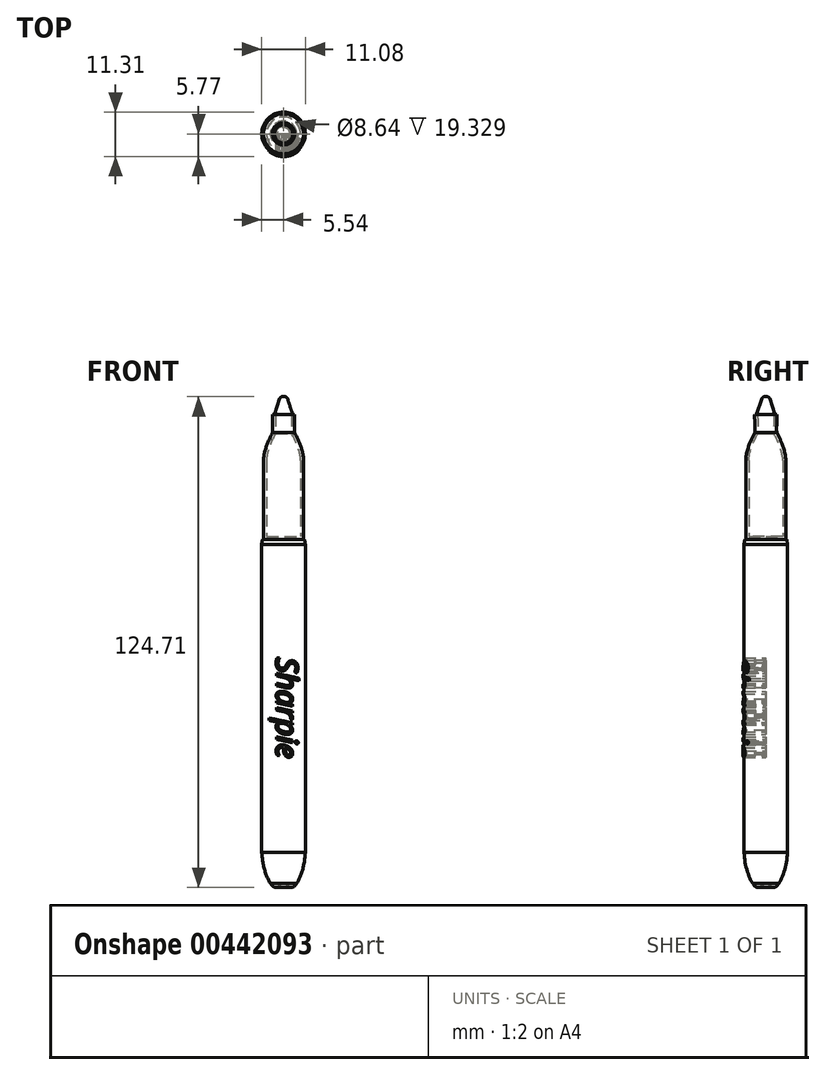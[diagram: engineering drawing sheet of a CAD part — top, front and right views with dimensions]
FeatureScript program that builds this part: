
annotation { "Feature Type Name" : "Feature", "Feature Type Description" : "" }
export const myFeature = defineFeature(function(context is Context, id is Id, definition is map)
    precondition{}
    {
        {
            var Q0;
            Q0=qCreatedBy(makeId("Right.planeOp"),FACE);
            var sketch = newSketch(context, id + "F0", { "sketchPlane" : qUnion([Q0])});
            skArc(sketch, "E0", {"start": v(1.65, 0) * mm, "mid": v(0.9, 0.63) * mm, "end": v(0, 1.02) * mm});
            skLineSegment(sketch, "E1", {"start": v(0, 0) * mm, "end": v(0, 15.3) * mm, "construction": true});
            skLineSegment(sketch, "E2", {"start": v(-4.14, 8.9) * mm, "end": v(12.15, 8.9) * mm, "construction": true});
            skLineSegment(sketch, "E3", {"start": v(5.54, -3.16) * mm, "end": v(5.54, 13.42) * mm, "construction": true});
            skLineSegment(sketch, "E4", {"start": v(3.31, 16.2) * mm, "end": v(3.31, -2.19) * mm, "construction": true});
            skFitSpline(sketch, "E5", {"points": [v(1.65, 0) * mm, v(3.31, 1.03) * mm], "startDerivative": vector(2.74, 0) * mm, "endDerivative": vector(1.4, 2.31) * mm});
            skFitSpline(sketch, "E6", {"points": [v(3.31, 1.03) * mm, v(5.54, 8.9) * mm], "startDerivative": vector(3.92, 5.98) * mm, "endDerivative": vector(0.67, 9.24) * mm});
            skLineSegment(sketch, "E7", {"start": v(-15.24, 87.12) * mm, "end": v(35.45, 87.12) * mm, "construction": true});
            skLineSegment(sketch, "E8", {"start": v(5.54, 8.9) * mm, "end": v(5.54, 87.12) * mm});
            skPoint(sketch, "E8.endSnap0", {"position": v(10.1, 87.12) * mm});
            skLineSegment(sketch, "E9", {"start": v(5.54, 87.12) * mm, "end": v(5.33, 88.38) * mm});
            skLineSegment(sketch, "E10", {"start": v(5.33, 88.38) * mm, "end": v(0, 88.38) * mm});
            skLineSegment(sketch, "E11", {"start": v(0, 88.38) * mm, "end": v(0, 1.02) * mm});
            skSolve(sketch);
        }
        {
            var Q0;
            Q0=qSketchRegion(id+"F0",true);
            var Q1;
            Q1=sQuery(id+"F0.wireOp",EDGE,"E11");
            revolve(context, id + "F1", {"entities" : qUnion([Q0]), "axis" : qUnion([Q1]), "revolveType" : RevolveType.FULL});
        }
        {
            var Q0;
            Q0=qCreatedBy(makeId("Front.planeOp"),FACE);
            var sketch = newSketch(context, id + "F2", { "sketchPlane" : qUnion([Q0])});
            skLineSegment(sketch, "E12", {"start": v(0, 88.38) * mm, "end": v(0, 120.13) * mm});
            skLineSegment(sketch, "E13", {"start": v(0, 120.13) * mm, "end": v(2.8, 120.13) * mm});
            skLineSegment(sketch, "E14", {"start": v(-7.77, 108.47) * mm, "end": v(20.65, 108.47) * mm, "construction": true});
            skLineSegment(sketch, "E15", {"start": v(5.08, 128.73) * mm, "end": v(5.08, 79.74) * mm, "construction": true});
            skLineSegment(sketch, "E16", {"start": v(5.08, 79.74) * mm, "end": v(5.61, 79.74) * mm, "construction": true});
            skLineSegment(sketch, "E17", {"start": v(0, 88.38) * mm, "end": v(5.08, 88.38) * mm});
            skLineSegment(sketch, "E18", {"start": v(5.08, 88.38) * mm, "end": v(5.08, 108.47) * mm});
            skFitSpline(sketch, "E19", {"points": [v(2.8, 115.55) * mm, v(5.08, 108.47) * mm], "startDerivative": vector(4.16, -7.76) * mm, "endDerivative": vector(0, -5.98) * mm});
            skFitSpline(sketch, "E20", {"points": [v(2.8, 120.13) * mm, v(2.8, 115.55) * mm], "startDerivative": vector(0.35, -1.11) * mm, "endDerivative": vector(0.39, -3.2) * mm});
            skSolve(sketch);
        }
        {
            var Q0;
            Q0=makeQuery(id+"F2.imprint","IMPRINT",FACE,{"disambiguationData":[TD([[makeQuery(id+"F2.imprint","IMPRINT",EDGE,{"derivedFrom":sQuery(id+"F2.wireOp",EDGE,"E12")}),-1.0]])]});
            var Q1;
            Q1=sQuery(id+"F2.wireOp",EDGE,"E12");
            revolve(context, id + "F3", {"entities" : qUnion([Q0]), "axis" : qUnion([Q1]), "revolveType" : RevolveType.FULL});
        }
        {
            var Q0;
            Q0=makeQuery(id+"F3.opRevolve","SWEPT_FACE",FACE,{"disambiguationData":[OSD([sQuery(id+"F2.wireOp",EDGE,"E13")])]});
            shell(context, id + "F4", {"entities" : qUnion([Q0]), "thickness" : 0.76 * mm});
        }
        {
            var Q0;
            Q0=qCreatedBy(makeId("Front.planeOp"),FACE);
            var sketch = newSketch(context, id + "F5", { "sketchPlane" : qUnion([Q0])});
            skText(sketch, "E21", { "text": "Sharpie", "fontName": "OpenSans-Italic.ttf"});
            const initialGuessF5  = {"E21": [-0.00997, 0.02356, 1, 0, 0.00548]};
            skSetInitialGuess(sketch, initialGuessF5);
            skSolve(sketch);
        }
        {
            var Q0;
            Q0=qSketchRegion(id+"F5",true);
            extrude(context, id + "F6", {"entities" : qUnion([Q0]), "depth" : 6.35 * mm});
        }
        {
            var Q0;
            Q0=qCreatedBy(makeId("Front.planeOp"),FACE);
            var sketch = newSketch(context, id + "F7", { "sketchPlane" : qUnion([Q0])});
            skLineSegment(sketch, "E22", {"start": v(0, 0) * mm, "end": v(0, 153.56) * mm, "construction": true});
            skLineSegment(sketch, "E23", {"start": v(0, 0) * mm, "end": v(-98.51, 0) * mm, "construction": true});
            skSolve(sketch);
        }
        {
            var Q0;
            Q0=qCreatedBy(makeId("Top.planeOp"),FACE);
            var sketch = newSketch(context, id + "F8", { "sketchPlane" : qUnion([Q0])});
            skLineSegment(sketch, "E24", {"start": v(0, 0) * mm, "end": v(0, 70.55) * mm, "construction": true});
            skSolve(sketch);
        }
        {
            var Q0;
            Q0=makeQuery(id+"F6.opExtrude","SWEPT_BODY",BODY,{"disambiguationData":[OSD([sQuery(id+"F5.wireOp",EDGE,"E21.sketch_text.stroke-126"),sQuery(id+"F5.wireOp",EDGE,"E21.sketch_text.stroke-127"),sQuery(id+"F5.wireOp",EDGE,"E21.sketch_text.stroke-128"),sQuery(id+"F5.wireOp",EDGE,"E21.sketch_text.stroke-129"),sQuery(id+"F5.wireOp",EDGE,"E21.sketch_text.stroke-130"),sQuery(id+"F5.wireOp",EDGE,"E21.sketch_text.stroke-131"),sQuery(id+"F5.wireOp",EDGE,"E21.sketch_text.stroke-132"),sQuery(id+"F5.wireOp",EDGE,"E21.sketch_text.stroke-133"),sQuery(id+"F5.wireOp",EDGE,"E21.sketch_text.stroke-134"),sQuery(id+"F5.wireOp",EDGE,"E21.sketch_text.stroke-135"),sQuery(id+"F5.wireOp",EDGE,"E21.sketch_text.stroke-136"),sQuery(id+"F5.wireOp",EDGE,"E21.sketch_text.stroke-137"),sQuery(id+"F5.wireOp",EDGE,"E21.sketch_text.stroke-138"),sQuery(id+"F5.wireOp",EDGE,"E21.sketch_text.stroke-139"),sQuery(id+"F5.wireOp",EDGE,"E21.sketch_text.stroke-140"),sQuery(id+"F5.wireOp",EDGE,"E21.sketch_text.stroke-141"),sQuery(id+"F5.wireOp",EDGE,"E21.sketch_text.stroke-142"),sQuery(id+"F5.wireOp",EDGE,"E21.sketch_text.stroke-143"),sQuery(id+"F5.wireOp",EDGE,"E21.sketch_text.stroke-144"),sQuery(id+"F5.wireOp",EDGE,"E21.sketch_text.stroke-145"),sQuery(id+"F5.wireOp",EDGE,"E21.sketch_text.stroke-146"),sQuery(id+"F5.wireOp",EDGE,"E21.sketch_text.stroke-147"),sQuery(id+"F5.wireOp",EDGE,"E21.sketch_text.stroke-148"),sQuery(id+"F5.wireOp",EDGE,"E21.sketch_text.stroke-149"),sQuery(id+"F5.wireOp",EDGE,"E21.sketch_text.stroke-150")])]});
            var Q1;
            Q1=makeQuery(id+"F6.opExtrude","SWEPT_BODY",BODY,{"disambiguationData":[OSD([sQuery(id+"F5.wireOp",EDGE,"E21.sketch_text.stroke-119"),sQuery(id+"F5.wireOp",EDGE,"E21.sketch_text.stroke-120"),sQuery(id+"F5.wireOp",EDGE,"E21.sketch_text.stroke-121"),sQuery(id+"F5.wireOp",EDGE,"E21.sketch_text.stroke-122"),sQuery(id+"F5.wireOp",EDGE,"E21.sketch_text.stroke-123"),sQuery(id+"F5.wireOp",EDGE,"E21.sketch_text.stroke-124"),sQuery(id+"F5.wireOp",EDGE,"E21.sketch_text.stroke-125")])]});
            var Q2;
            Q2=makeQuery(id+"F6.opExtrude","SWEPT_BODY",BODY,{"disambiguationData":[OSD([sQuery(id+"F5.wireOp",EDGE,"E21.sketch_text.stroke-115"),sQuery(id+"F5.wireOp",EDGE,"E21.sketch_text.stroke-116"),sQuery(id+"F5.wireOp",EDGE,"E21.sketch_text.stroke-117"),sQuery(id+"F5.wireOp",EDGE,"E21.sketch_text.stroke-118")])]});
            var Q3;
            Q3=makeQuery(id+"F6.opExtrude","SWEPT_BODY",BODY,{"disambiguationData":[OSD([sQuery(id+"F5.wireOp",EDGE,"E21.sketch_text.stroke-89"),sQuery(id+"F5.wireOp",EDGE,"E21.sketch_text.stroke-90"),sQuery(id+"F5.wireOp",EDGE,"E21.sketch_text.stroke-91"),sQuery(id+"F5.wireOp",EDGE,"E21.sketch_text.stroke-92"),sQuery(id+"F5.wireOp",EDGE,"E21.sketch_text.stroke-93"),sQuery(id+"F5.wireOp",EDGE,"E21.sketch_text.stroke-94"),sQuery(id+"F5.wireOp",EDGE,"E21.sketch_text.stroke-95"),sQuery(id+"F5.wireOp",EDGE,"E21.sketch_text.stroke-96"),sQuery(id+"F5.wireOp",EDGE,"E21.sketch_text.stroke-97"),sQuery(id+"F5.wireOp",EDGE,"E21.sketch_text.stroke-98"),sQuery(id+"F5.wireOp",EDGE,"E21.sketch_text.stroke-99"),sQuery(id+"F5.wireOp",EDGE,"E21.sketch_text.stroke-100"),sQuery(id+"F5.wireOp",EDGE,"E21.sketch_text.stroke-101"),sQuery(id+"F5.wireOp",EDGE,"E21.sketch_text.stroke-102"),sQuery(id+"F5.wireOp",EDGE,"E21.sketch_text.stroke-103"),sQuery(id+"F5.wireOp",EDGE,"E21.sketch_text.stroke-104"),sQuery(id+"F5.wireOp",EDGE,"E21.sketch_text.stroke-105"),sQuery(id+"F5.wireOp",EDGE,"E21.sketch_text.stroke-106"),sQuery(id+"F5.wireOp",EDGE,"E21.sketch_text.stroke-107"),sQuery(id+"F5.wireOp",EDGE,"E21.sketch_text.stroke-108"),sQuery(id+"F5.wireOp",EDGE,"E21.sketch_text.stroke-109"),sQuery(id+"F5.wireOp",EDGE,"E21.sketch_text.stroke-110"),sQuery(id+"F5.wireOp",EDGE,"E21.sketch_text.stroke-111"),sQuery(id+"F5.wireOp",EDGE,"E21.sketch_text.stroke-112"),sQuery(id+"F5.wireOp",EDGE,"E21.sketch_text.stroke-113"),sQuery(id+"F5.wireOp",EDGE,"E21.sketch_text.stroke-114")])]});
            var Q4;
            Q4=makeQuery(id+"F6.opExtrude","SWEPT_BODY",BODY,{"disambiguationData":[OSD([sQuery(id+"F5.wireOp",EDGE,"E21.sketch_text.stroke-74"),sQuery(id+"F5.wireOp",EDGE,"E21.sketch_text.stroke-75"),sQuery(id+"F5.wireOp",EDGE,"E21.sketch_text.stroke-76"),sQuery(id+"F5.wireOp",EDGE,"E21.sketch_text.stroke-77"),sQuery(id+"F5.wireOp",EDGE,"E21.sketch_text.stroke-78"),sQuery(id+"F5.wireOp",EDGE,"E21.sketch_text.stroke-79"),sQuery(id+"F5.wireOp",EDGE,"E21.sketch_text.stroke-80"),sQuery(id+"F5.wireOp",EDGE,"E21.sketch_text.stroke-81"),sQuery(id+"F5.wireOp",EDGE,"E21.sketch_text.stroke-82"),sQuery(id+"F5.wireOp",EDGE,"E21.sketch_text.stroke-83"),sQuery(id+"F5.wireOp",EDGE,"E21.sketch_text.stroke-84"),sQuery(id+"F5.wireOp",EDGE,"E21.sketch_text.stroke-85"),sQuery(id+"F5.wireOp",EDGE,"E21.sketch_text.stroke-86"),sQuery(id+"F5.wireOp",EDGE,"E21.sketch_text.stroke-87"),sQuery(id+"F5.wireOp",EDGE,"E21.sketch_text.stroke-88")])]});
            var Q5;
            Q5=makeQuery(id+"F6.opExtrude","SWEPT_BODY",BODY,{"disambiguationData":[OSD([sQuery(id+"F5.wireOp",EDGE,"E21.sketch_text.stroke-49"),sQuery(id+"F5.wireOp",EDGE,"E21.sketch_text.stroke-50"),sQuery(id+"F5.wireOp",EDGE,"E21.sketch_text.stroke-51"),sQuery(id+"F5.wireOp",EDGE,"E21.sketch_text.stroke-52"),sQuery(id+"F5.wireOp",EDGE,"E21.sketch_text.stroke-53"),sQuery(id+"F5.wireOp",EDGE,"E21.sketch_text.stroke-54"),sQuery(id+"F5.wireOp",EDGE,"E21.sketch_text.stroke-55"),sQuery(id+"F5.wireOp",EDGE,"E21.sketch_text.stroke-56"),sQuery(id+"F5.wireOp",EDGE,"E21.sketch_text.stroke-57"),sQuery(id+"F5.wireOp",EDGE,"E21.sketch_text.stroke-58"),sQuery(id+"F5.wireOp",EDGE,"E21.sketch_text.stroke-59"),sQuery(id+"F5.wireOp",EDGE,"E21.sketch_text.stroke-60"),sQuery(id+"F5.wireOp",EDGE,"E21.sketch_text.stroke-61"),sQuery(id+"F5.wireOp",EDGE,"E21.sketch_text.stroke-62"),sQuery(id+"F5.wireOp",EDGE,"E21.sketch_text.stroke-63"),sQuery(id+"F5.wireOp",EDGE,"E21.sketch_text.stroke-64"),sQuery(id+"F5.wireOp",EDGE,"E21.sketch_text.stroke-65"),sQuery(id+"F5.wireOp",EDGE,"E21.sketch_text.stroke-66"),sQuery(id+"F5.wireOp",EDGE,"E21.sketch_text.stroke-67"),sQuery(id+"F5.wireOp",EDGE,"E21.sketch_text.stroke-68"),sQuery(id+"F5.wireOp",EDGE,"E21.sketch_text.stroke-69"),sQuery(id+"F5.wireOp",EDGE,"E21.sketch_text.stroke-70"),sQuery(id+"F5.wireOp",EDGE,"E21.sketch_text.stroke-71"),sQuery(id+"F5.wireOp",EDGE,"E21.sketch_text.stroke-72"),sQuery(id+"F5.wireOp",EDGE,"E21.sketch_text.stroke-73")])]});
            var Q6;
            Q6=makeQuery(id+"F6.opExtrude","SWEPT_BODY",BODY,{"disambiguationData":[OSD([sQuery(id+"F5.wireOp",EDGE,"E21.sketch_text.stroke-27"),sQuery(id+"F5.wireOp",EDGE,"E21.sketch_text.stroke-28"),sQuery(id+"F5.wireOp",EDGE,"E21.sketch_text.stroke-29"),sQuery(id+"F5.wireOp",EDGE,"E21.sketch_text.stroke-30"),sQuery(id+"F5.wireOp",EDGE,"E21.sketch_text.stroke-31"),sQuery(id+"F5.wireOp",EDGE,"E21.sketch_text.stroke-32"),sQuery(id+"F5.wireOp",EDGE,"E21.sketch_text.stroke-33"),sQuery(id+"F5.wireOp",EDGE,"E21.sketch_text.stroke-34"),sQuery(id+"F5.wireOp",EDGE,"E21.sketch_text.stroke-35"),sQuery(id+"F5.wireOp",EDGE,"E21.sketch_text.stroke-36"),sQuery(id+"F5.wireOp",EDGE,"E21.sketch_text.stroke-37"),sQuery(id+"F5.wireOp",EDGE,"E21.sketch_text.stroke-38"),sQuery(id+"F5.wireOp",EDGE,"E21.sketch_text.stroke-39"),sQuery(id+"F5.wireOp",EDGE,"E21.sketch_text.stroke-40"),sQuery(id+"F5.wireOp",EDGE,"E21.sketch_text.stroke-41"),sQuery(id+"F5.wireOp",EDGE,"E21.sketch_text.stroke-42"),sQuery(id+"F5.wireOp",EDGE,"E21.sketch_text.stroke-43"),sQuery(id+"F5.wireOp",EDGE,"E21.sketch_text.stroke-44"),sQuery(id+"F5.wireOp",EDGE,"E21.sketch_text.stroke-45"),sQuery(id+"F5.wireOp",EDGE,"E21.sketch_text.stroke-46"),sQuery(id+"F5.wireOp",EDGE,"E21.sketch_text.stroke-47"),sQuery(id+"F5.wireOp",EDGE,"E21.sketch_text.stroke-48")])]});
            var Q7;
            Q7=makeQuery(id+"F6.opExtrude","SWEPT_BODY",BODY,{"disambiguationData":[OSD([sQuery(id+"F5.wireOp",EDGE,"E21.sketch_text.stroke-0"),sQuery(id+"F5.wireOp",EDGE,"E21.sketch_text.stroke-1"),sQuery(id+"F5.wireOp",EDGE,"E21.sketch_text.stroke-2"),sQuery(id+"F5.wireOp",EDGE,"E21.sketch_text.stroke-3"),sQuery(id+"F5.wireOp",EDGE,"E21.sketch_text.stroke-4"),sQuery(id+"F5.wireOp",EDGE,"E21.sketch_text.stroke-5"),sQuery(id+"F5.wireOp",EDGE,"E21.sketch_text.stroke-6"),sQuery(id+"F5.wireOp",EDGE,"E21.sketch_text.stroke-7"),sQuery(id+"F5.wireOp",EDGE,"E21.sketch_text.stroke-8"),sQuery(id+"F5.wireOp",EDGE,"E21.sketch_text.stroke-9"),sQuery(id+"F5.wireOp",EDGE,"E21.sketch_text.stroke-10"),sQuery(id+"F5.wireOp",EDGE,"E21.sketch_text.stroke-11"),sQuery(id+"F5.wireOp",EDGE,"E21.sketch_text.stroke-12"),sQuery(id+"F5.wireOp",EDGE,"E21.sketch_text.stroke-13"),sQuery(id+"F5.wireOp",EDGE,"E21.sketch_text.stroke-14"),sQuery(id+"F5.wireOp",EDGE,"E21.sketch_text.stroke-15"),sQuery(id+"F5.wireOp",EDGE,"E21.sketch_text.stroke-16"),sQuery(id+"F5.wireOp",EDGE,"E21.sketch_text.stroke-17"),sQuery(id+"F5.wireOp",EDGE,"E21.sketch_text.stroke-18"),sQuery(id+"F5.wireOp",EDGE,"E21.sketch_text.stroke-19"),sQuery(id+"F5.wireOp",EDGE,"E21.sketch_text.stroke-20"),sQuery(id+"F5.wireOp",EDGE,"E21.sketch_text.stroke-21"),sQuery(id+"F5.wireOp",EDGE,"E21.sketch_text.stroke-22"),sQuery(id+"F5.wireOp",EDGE,"E21.sketch_text.stroke-23"),sQuery(id+"F5.wireOp",EDGE,"E21.sketch_text.stroke-24"),sQuery(id+"F5.wireOp",EDGE,"E21.sketch_text.stroke-25"),sQuery(id+"F5.wireOp",EDGE,"E21.sketch_text.stroke-26")])]});
            var Q8;
            Q8=sQuery(id+"F8.wireOp",EDGE,"E24");
            transform(context, id + "F9", {"entities" : qUnion([Q0, Q1, Q2, Q3, Q4, Q5, Q6, Q7]), "transformType" : TransformType.ROTATION, "transformAxis" : qUnion([Q8]), "angle" : 90 * degree, "makeCopy" : false});
        }
        {
            var Q0;
            Q0=makeQuery(id+"F6.opExtrude","SWEPT_BODY",BODY,{"disambiguationData":[OSD([sQuery(id+"F5.wireOp",EDGE,"E21.sketch_text.stroke-0"),sQuery(id+"F5.wireOp",EDGE,"E21.sketch_text.stroke-1"),sQuery(id+"F5.wireOp",EDGE,"E21.sketch_text.stroke-2"),sQuery(id+"F5.wireOp",EDGE,"E21.sketch_text.stroke-3"),sQuery(id+"F5.wireOp",EDGE,"E21.sketch_text.stroke-4"),sQuery(id+"F5.wireOp",EDGE,"E21.sketch_text.stroke-5"),sQuery(id+"F5.wireOp",EDGE,"E21.sketch_text.stroke-6"),sQuery(id+"F5.wireOp",EDGE,"E21.sketch_text.stroke-7"),sQuery(id+"F5.wireOp",EDGE,"E21.sketch_text.stroke-8"),sQuery(id+"F5.wireOp",EDGE,"E21.sketch_text.stroke-9"),sQuery(id+"F5.wireOp",EDGE,"E21.sketch_text.stroke-10"),sQuery(id+"F5.wireOp",EDGE,"E21.sketch_text.stroke-11"),sQuery(id+"F5.wireOp",EDGE,"E21.sketch_text.stroke-12"),sQuery(id+"F5.wireOp",EDGE,"E21.sketch_text.stroke-13"),sQuery(id+"F5.wireOp",EDGE,"E21.sketch_text.stroke-14"),sQuery(id+"F5.wireOp",EDGE,"E21.sketch_text.stroke-15"),sQuery(id+"F5.wireOp",EDGE,"E21.sketch_text.stroke-16"),sQuery(id+"F5.wireOp",EDGE,"E21.sketch_text.stroke-17"),sQuery(id+"F5.wireOp",EDGE,"E21.sketch_text.stroke-18"),sQuery(id+"F5.wireOp",EDGE,"E21.sketch_text.stroke-19"),sQuery(id+"F5.wireOp",EDGE,"E21.sketch_text.stroke-20"),sQuery(id+"F5.wireOp",EDGE,"E21.sketch_text.stroke-21"),sQuery(id+"F5.wireOp",EDGE,"E21.sketch_text.stroke-22"),sQuery(id+"F5.wireOp",EDGE,"E21.sketch_text.stroke-23"),sQuery(id+"F5.wireOp",EDGE,"E21.sketch_text.stroke-24"),sQuery(id+"F5.wireOp",EDGE,"E21.sketch_text.stroke-25"),sQuery(id+"F5.wireOp",EDGE,"E21.sketch_text.stroke-26")])]});
            var Q1;
            Q1=makeQuery(id+"F6.opExtrude","SWEPT_BODY",BODY,{"disambiguationData":[OSD([sQuery(id+"F5.wireOp",EDGE,"E21.sketch_text.stroke-27"),sQuery(id+"F5.wireOp",EDGE,"E21.sketch_text.stroke-28"),sQuery(id+"F5.wireOp",EDGE,"E21.sketch_text.stroke-29"),sQuery(id+"F5.wireOp",EDGE,"E21.sketch_text.stroke-30"),sQuery(id+"F5.wireOp",EDGE,"E21.sketch_text.stroke-31"),sQuery(id+"F5.wireOp",EDGE,"E21.sketch_text.stroke-32"),sQuery(id+"F5.wireOp",EDGE,"E21.sketch_text.stroke-33"),sQuery(id+"F5.wireOp",EDGE,"E21.sketch_text.stroke-34"),sQuery(id+"F5.wireOp",EDGE,"E21.sketch_text.stroke-35"),sQuery(id+"F5.wireOp",EDGE,"E21.sketch_text.stroke-36"),sQuery(id+"F5.wireOp",EDGE,"E21.sketch_text.stroke-37"),sQuery(id+"F5.wireOp",EDGE,"E21.sketch_text.stroke-38"),sQuery(id+"F5.wireOp",EDGE,"E21.sketch_text.stroke-39"),sQuery(id+"F5.wireOp",EDGE,"E21.sketch_text.stroke-40"),sQuery(id+"F5.wireOp",EDGE,"E21.sketch_text.stroke-41"),sQuery(id+"F5.wireOp",EDGE,"E21.sketch_text.stroke-42"),sQuery(id+"F5.wireOp",EDGE,"E21.sketch_text.stroke-43"),sQuery(id+"F5.wireOp",EDGE,"E21.sketch_text.stroke-44"),sQuery(id+"F5.wireOp",EDGE,"E21.sketch_text.stroke-45"),sQuery(id+"F5.wireOp",EDGE,"E21.sketch_text.stroke-46"),sQuery(id+"F5.wireOp",EDGE,"E21.sketch_text.stroke-47"),sQuery(id+"F5.wireOp",EDGE,"E21.sketch_text.stroke-48")])]});
            var Q2;
            Q2=makeQuery(id+"F6.opExtrude","SWEPT_BODY",BODY,{"disambiguationData":[OSD([sQuery(id+"F5.wireOp",EDGE,"E21.sketch_text.stroke-49"),sQuery(id+"F5.wireOp",EDGE,"E21.sketch_text.stroke-50"),sQuery(id+"F5.wireOp",EDGE,"E21.sketch_text.stroke-51"),sQuery(id+"F5.wireOp",EDGE,"E21.sketch_text.stroke-52"),sQuery(id+"F5.wireOp",EDGE,"E21.sketch_text.stroke-53"),sQuery(id+"F5.wireOp",EDGE,"E21.sketch_text.stroke-54"),sQuery(id+"F5.wireOp",EDGE,"E21.sketch_text.stroke-55"),sQuery(id+"F5.wireOp",EDGE,"E21.sketch_text.stroke-56"),sQuery(id+"F5.wireOp",EDGE,"E21.sketch_text.stroke-57"),sQuery(id+"F5.wireOp",EDGE,"E21.sketch_text.stroke-58"),sQuery(id+"F5.wireOp",EDGE,"E21.sketch_text.stroke-59"),sQuery(id+"F5.wireOp",EDGE,"E21.sketch_text.stroke-60"),sQuery(id+"F5.wireOp",EDGE,"E21.sketch_text.stroke-61"),sQuery(id+"F5.wireOp",EDGE,"E21.sketch_text.stroke-62"),sQuery(id+"F5.wireOp",EDGE,"E21.sketch_text.stroke-63"),sQuery(id+"F5.wireOp",EDGE,"E21.sketch_text.stroke-64"),sQuery(id+"F5.wireOp",EDGE,"E21.sketch_text.stroke-65"),sQuery(id+"F5.wireOp",EDGE,"E21.sketch_text.stroke-66"),sQuery(id+"F5.wireOp",EDGE,"E21.sketch_text.stroke-67"),sQuery(id+"F5.wireOp",EDGE,"E21.sketch_text.stroke-68"),sQuery(id+"F5.wireOp",EDGE,"E21.sketch_text.stroke-69"),sQuery(id+"F5.wireOp",EDGE,"E21.sketch_text.stroke-70"),sQuery(id+"F5.wireOp",EDGE,"E21.sketch_text.stroke-71"),sQuery(id+"F5.wireOp",EDGE,"E21.sketch_text.stroke-72"),sQuery(id+"F5.wireOp",EDGE,"E21.sketch_text.stroke-73")])]});
            var Q3;
            Q3=makeQuery(id+"F6.opExtrude","SWEPT_BODY",BODY,{"disambiguationData":[OSD([sQuery(id+"F5.wireOp",EDGE,"E21.sketch_text.stroke-74"),sQuery(id+"F5.wireOp",EDGE,"E21.sketch_text.stroke-75"),sQuery(id+"F5.wireOp",EDGE,"E21.sketch_text.stroke-76"),sQuery(id+"F5.wireOp",EDGE,"E21.sketch_text.stroke-77"),sQuery(id+"F5.wireOp",EDGE,"E21.sketch_text.stroke-78"),sQuery(id+"F5.wireOp",EDGE,"E21.sketch_text.stroke-79"),sQuery(id+"F5.wireOp",EDGE,"E21.sketch_text.stroke-80"),sQuery(id+"F5.wireOp",EDGE,"E21.sketch_text.stroke-81"),sQuery(id+"F5.wireOp",EDGE,"E21.sketch_text.stroke-82"),sQuery(id+"F5.wireOp",EDGE,"E21.sketch_text.stroke-83"),sQuery(id+"F5.wireOp",EDGE,"E21.sketch_text.stroke-84"),sQuery(id+"F5.wireOp",EDGE,"E21.sketch_text.stroke-85"),sQuery(id+"F5.wireOp",EDGE,"E21.sketch_text.stroke-86"),sQuery(id+"F5.wireOp",EDGE,"E21.sketch_text.stroke-87"),sQuery(id+"F5.wireOp",EDGE,"E21.sketch_text.stroke-88")])]});
            var Q4;
            Q4=makeQuery(id+"F6.opExtrude","SWEPT_BODY",BODY,{"disambiguationData":[OSD([sQuery(id+"F5.wireOp",EDGE,"E21.sketch_text.stroke-89"),sQuery(id+"F5.wireOp",EDGE,"E21.sketch_text.stroke-90"),sQuery(id+"F5.wireOp",EDGE,"E21.sketch_text.stroke-91"),sQuery(id+"F5.wireOp",EDGE,"E21.sketch_text.stroke-92"),sQuery(id+"F5.wireOp",EDGE,"E21.sketch_text.stroke-93"),sQuery(id+"F5.wireOp",EDGE,"E21.sketch_text.stroke-94"),sQuery(id+"F5.wireOp",EDGE,"E21.sketch_text.stroke-95"),sQuery(id+"F5.wireOp",EDGE,"E21.sketch_text.stroke-96"),sQuery(id+"F5.wireOp",EDGE,"E21.sketch_text.stroke-97"),sQuery(id+"F5.wireOp",EDGE,"E21.sketch_text.stroke-98"),sQuery(id+"F5.wireOp",EDGE,"E21.sketch_text.stroke-99"),sQuery(id+"F5.wireOp",EDGE,"E21.sketch_text.stroke-100"),sQuery(id+"F5.wireOp",EDGE,"E21.sketch_text.stroke-101"),sQuery(id+"F5.wireOp",EDGE,"E21.sketch_text.stroke-102"),sQuery(id+"F5.wireOp",EDGE,"E21.sketch_text.stroke-103"),sQuery(id+"F5.wireOp",EDGE,"E21.sketch_text.stroke-104"),sQuery(id+"F5.wireOp",EDGE,"E21.sketch_text.stroke-105"),sQuery(id+"F5.wireOp",EDGE,"E21.sketch_text.stroke-106"),sQuery(id+"F5.wireOp",EDGE,"E21.sketch_text.stroke-107"),sQuery(id+"F5.wireOp",EDGE,"E21.sketch_text.stroke-108"),sQuery(id+"F5.wireOp",EDGE,"E21.sketch_text.stroke-109"),sQuery(id+"F5.wireOp",EDGE,"E21.sketch_text.stroke-110"),sQuery(id+"F5.wireOp",EDGE,"E21.sketch_text.stroke-111"),sQuery(id+"F5.wireOp",EDGE,"E21.sketch_text.stroke-112"),sQuery(id+"F5.wireOp",EDGE,"E21.sketch_text.stroke-113"),sQuery(id+"F5.wireOp",EDGE,"E21.sketch_text.stroke-114")])]});
            var Q5;
            Q5=makeQuery(id+"F6.opExtrude","SWEPT_BODY",BODY,{"disambiguationData":[OSD([sQuery(id+"F5.wireOp",EDGE,"E21.sketch_text.stroke-115"),sQuery(id+"F5.wireOp",EDGE,"E21.sketch_text.stroke-116"),sQuery(id+"F5.wireOp",EDGE,"E21.sketch_text.stroke-117"),sQuery(id+"F5.wireOp",EDGE,"E21.sketch_text.stroke-118")])]});
            var Q6;
            Q6=makeQuery(id+"F6.opExtrude","SWEPT_BODY",BODY,{"disambiguationData":[OSD([sQuery(id+"F5.wireOp",EDGE,"E21.sketch_text.stroke-119"),sQuery(id+"F5.wireOp",EDGE,"E21.sketch_text.stroke-120"),sQuery(id+"F5.wireOp",EDGE,"E21.sketch_text.stroke-121"),sQuery(id+"F5.wireOp",EDGE,"E21.sketch_text.stroke-122"),sQuery(id+"F5.wireOp",EDGE,"E21.sketch_text.stroke-123"),sQuery(id+"F5.wireOp",EDGE,"E21.sketch_text.stroke-124"),sQuery(id+"F5.wireOp",EDGE,"E21.sketch_text.stroke-125")])]});
            var Q7;
            Q7=makeQuery(id+"F6.opExtrude","SWEPT_BODY",BODY,{"disambiguationData":[OSD([sQuery(id+"F5.wireOp",EDGE,"E21.sketch_text.stroke-126"),sQuery(id+"F5.wireOp",EDGE,"E21.sketch_text.stroke-127"),sQuery(id+"F5.wireOp",EDGE,"E21.sketch_text.stroke-128"),sQuery(id+"F5.wireOp",EDGE,"E21.sketch_text.stroke-129"),sQuery(id+"F5.wireOp",EDGE,"E21.sketch_text.stroke-130"),sQuery(id+"F5.wireOp",EDGE,"E21.sketch_text.stroke-131"),sQuery(id+"F5.wireOp",EDGE,"E21.sketch_text.stroke-132"),sQuery(id+"F5.wireOp",EDGE,"E21.sketch_text.stroke-133"),sQuery(id+"F5.wireOp",EDGE,"E21.sketch_text.stroke-134"),sQuery(id+"F5.wireOp",EDGE,"E21.sketch_text.stroke-135"),sQuery(id+"F5.wireOp",EDGE,"E21.sketch_text.stroke-136"),sQuery(id+"F5.wireOp",EDGE,"E21.sketch_text.stroke-137"),sQuery(id+"F5.wireOp",EDGE,"E21.sketch_text.stroke-138"),sQuery(id+"F5.wireOp",EDGE,"E21.sketch_text.stroke-139"),sQuery(id+"F5.wireOp",EDGE,"E21.sketch_text.stroke-140"),sQuery(id+"F5.wireOp",EDGE,"E21.sketch_text.stroke-141"),sQuery(id+"F5.wireOp",EDGE,"E21.sketch_text.stroke-142"),sQuery(id+"F5.wireOp",EDGE,"E21.sketch_text.stroke-143"),sQuery(id+"F5.wireOp",EDGE,"E21.sketch_text.stroke-144"),sQuery(id+"F5.wireOp",EDGE,"E21.sketch_text.stroke-145"),sQuery(id+"F5.wireOp",EDGE,"E21.sketch_text.stroke-146"),sQuery(id+"F5.wireOp",EDGE,"E21.sketch_text.stroke-147"),sQuery(id+"F5.wireOp",EDGE,"E21.sketch_text.stroke-148"),sQuery(id+"F5.wireOp",EDGE,"E21.sketch_text.stroke-149"),sQuery(id+"F5.wireOp",EDGE,"E21.sketch_text.stroke-150")])]});
            var Q8;
            Q8=sQuery(id+"F7.wireOp",EDGE,"E22");
            transform(context, id + "F10", {"entities" : qUnion([Q0, Q1, Q2, Q3, Q4, Q5, Q6, Q7]), "transformType" : TransformType.TRANSLATION_DISTANCE, "transformDirection" : qUnion([Q8]), "distance" : 48.47 * mm, "makeCopy" : false});
        }
        {
            var Q0;
            Q0=makeQuery(id+"F6.opExtrude","SWEPT_BODY",BODY,{"disambiguationData":[OSD([sQuery(id+"F5.wireOp",EDGE,"E21.sketch_text.stroke-126"),sQuery(id+"F5.wireOp",EDGE,"E21.sketch_text.stroke-127"),sQuery(id+"F5.wireOp",EDGE,"E21.sketch_text.stroke-128"),sQuery(id+"F5.wireOp",EDGE,"E21.sketch_text.stroke-129"),sQuery(id+"F5.wireOp",EDGE,"E21.sketch_text.stroke-130"),sQuery(id+"F5.wireOp",EDGE,"E21.sketch_text.stroke-131"),sQuery(id+"F5.wireOp",EDGE,"E21.sketch_text.stroke-132"),sQuery(id+"F5.wireOp",EDGE,"E21.sketch_text.stroke-133"),sQuery(id+"F5.wireOp",EDGE,"E21.sketch_text.stroke-134"),sQuery(id+"F5.wireOp",EDGE,"E21.sketch_text.stroke-135"),sQuery(id+"F5.wireOp",EDGE,"E21.sketch_text.stroke-136"),sQuery(id+"F5.wireOp",EDGE,"E21.sketch_text.stroke-137"),sQuery(id+"F5.wireOp",EDGE,"E21.sketch_text.stroke-138"),sQuery(id+"F5.wireOp",EDGE,"E21.sketch_text.stroke-139"),sQuery(id+"F5.wireOp",EDGE,"E21.sketch_text.stroke-140"),sQuery(id+"F5.wireOp",EDGE,"E21.sketch_text.stroke-141"),sQuery(id+"F5.wireOp",EDGE,"E21.sketch_text.stroke-142"),sQuery(id+"F5.wireOp",EDGE,"E21.sketch_text.stroke-143"),sQuery(id+"F5.wireOp",EDGE,"E21.sketch_text.stroke-144"),sQuery(id+"F5.wireOp",EDGE,"E21.sketch_text.stroke-145"),sQuery(id+"F5.wireOp",EDGE,"E21.sketch_text.stroke-146"),sQuery(id+"F5.wireOp",EDGE,"E21.sketch_text.stroke-147"),sQuery(id+"F5.wireOp",EDGE,"E21.sketch_text.stroke-148"),sQuery(id+"F5.wireOp",EDGE,"E21.sketch_text.stroke-149"),sQuery(id+"F5.wireOp",EDGE,"E21.sketch_text.stroke-150")])]});
            var Q1;
            Q1=makeQuery(id+"F6.opExtrude","SWEPT_BODY",BODY,{"disambiguationData":[OSD([sQuery(id+"F5.wireOp",EDGE,"E21.sketch_text.stroke-119"),sQuery(id+"F5.wireOp",EDGE,"E21.sketch_text.stroke-120"),sQuery(id+"F5.wireOp",EDGE,"E21.sketch_text.stroke-121"),sQuery(id+"F5.wireOp",EDGE,"E21.sketch_text.stroke-122"),sQuery(id+"F5.wireOp",EDGE,"E21.sketch_text.stroke-123"),sQuery(id+"F5.wireOp",EDGE,"E21.sketch_text.stroke-124"),sQuery(id+"F5.wireOp",EDGE,"E21.sketch_text.stroke-125")])]});
            var Q2;
            Q2=makeQuery(id+"F6.opExtrude","SWEPT_BODY",BODY,{"disambiguationData":[OSD([sQuery(id+"F5.wireOp",EDGE,"E21.sketch_text.stroke-115"),sQuery(id+"F5.wireOp",EDGE,"E21.sketch_text.stroke-116"),sQuery(id+"F5.wireOp",EDGE,"E21.sketch_text.stroke-117"),sQuery(id+"F5.wireOp",EDGE,"E21.sketch_text.stroke-118")])]});
            var Q3;
            Q3=makeQuery(id+"F6.opExtrude","SWEPT_BODY",BODY,{"disambiguationData":[OSD([sQuery(id+"F5.wireOp",EDGE,"E21.sketch_text.stroke-89"),sQuery(id+"F5.wireOp",EDGE,"E21.sketch_text.stroke-90"),sQuery(id+"F5.wireOp",EDGE,"E21.sketch_text.stroke-91"),sQuery(id+"F5.wireOp",EDGE,"E21.sketch_text.stroke-92"),sQuery(id+"F5.wireOp",EDGE,"E21.sketch_text.stroke-93"),sQuery(id+"F5.wireOp",EDGE,"E21.sketch_text.stroke-94"),sQuery(id+"F5.wireOp",EDGE,"E21.sketch_text.stroke-95"),sQuery(id+"F5.wireOp",EDGE,"E21.sketch_text.stroke-96"),sQuery(id+"F5.wireOp",EDGE,"E21.sketch_text.stroke-97"),sQuery(id+"F5.wireOp",EDGE,"E21.sketch_text.stroke-98"),sQuery(id+"F5.wireOp",EDGE,"E21.sketch_text.stroke-99"),sQuery(id+"F5.wireOp",EDGE,"E21.sketch_text.stroke-100"),sQuery(id+"F5.wireOp",EDGE,"E21.sketch_text.stroke-101"),sQuery(id+"F5.wireOp",EDGE,"E21.sketch_text.stroke-102"),sQuery(id+"F5.wireOp",EDGE,"E21.sketch_text.stroke-103"),sQuery(id+"F5.wireOp",EDGE,"E21.sketch_text.stroke-104"),sQuery(id+"F5.wireOp",EDGE,"E21.sketch_text.stroke-105"),sQuery(id+"F5.wireOp",EDGE,"E21.sketch_text.stroke-106"),sQuery(id+"F5.wireOp",EDGE,"E21.sketch_text.stroke-107"),sQuery(id+"F5.wireOp",EDGE,"E21.sketch_text.stroke-108"),sQuery(id+"F5.wireOp",EDGE,"E21.sketch_text.stroke-109"),sQuery(id+"F5.wireOp",EDGE,"E21.sketch_text.stroke-110"),sQuery(id+"F5.wireOp",EDGE,"E21.sketch_text.stroke-111"),sQuery(id+"F5.wireOp",EDGE,"E21.sketch_text.stroke-112"),sQuery(id+"F5.wireOp",EDGE,"E21.sketch_text.stroke-113"),sQuery(id+"F5.wireOp",EDGE,"E21.sketch_text.stroke-114")])]});
            var Q4;
            Q4=makeQuery(id+"F6.opExtrude","SWEPT_BODY",BODY,{"disambiguationData":[OSD([sQuery(id+"F5.wireOp",EDGE,"E21.sketch_text.stroke-74"),sQuery(id+"F5.wireOp",EDGE,"E21.sketch_text.stroke-75"),sQuery(id+"F5.wireOp",EDGE,"E21.sketch_text.stroke-76"),sQuery(id+"F5.wireOp",EDGE,"E21.sketch_text.stroke-77"),sQuery(id+"F5.wireOp",EDGE,"E21.sketch_text.stroke-78"),sQuery(id+"F5.wireOp",EDGE,"E21.sketch_text.stroke-79"),sQuery(id+"F5.wireOp",EDGE,"E21.sketch_text.stroke-80"),sQuery(id+"F5.wireOp",EDGE,"E21.sketch_text.stroke-81"),sQuery(id+"F5.wireOp",EDGE,"E21.sketch_text.stroke-82"),sQuery(id+"F5.wireOp",EDGE,"E21.sketch_text.stroke-83"),sQuery(id+"F5.wireOp",EDGE,"E21.sketch_text.stroke-84"),sQuery(id+"F5.wireOp",EDGE,"E21.sketch_text.stroke-85"),sQuery(id+"F5.wireOp",EDGE,"E21.sketch_text.stroke-86"),sQuery(id+"F5.wireOp",EDGE,"E21.sketch_text.stroke-87"),sQuery(id+"F5.wireOp",EDGE,"E21.sketch_text.stroke-88")])]});
            var Q5;
            Q5=makeQuery(id+"F6.opExtrude","SWEPT_BODY",BODY,{"disambiguationData":[OSD([sQuery(id+"F5.wireOp",EDGE,"E21.sketch_text.stroke-49"),sQuery(id+"F5.wireOp",EDGE,"E21.sketch_text.stroke-50"),sQuery(id+"F5.wireOp",EDGE,"E21.sketch_text.stroke-51"),sQuery(id+"F5.wireOp",EDGE,"E21.sketch_text.stroke-52"),sQuery(id+"F5.wireOp",EDGE,"E21.sketch_text.stroke-53"),sQuery(id+"F5.wireOp",EDGE,"E21.sketch_text.stroke-54"),sQuery(id+"F5.wireOp",EDGE,"E21.sketch_text.stroke-55"),sQuery(id+"F5.wireOp",EDGE,"E21.sketch_text.stroke-56"),sQuery(id+"F5.wireOp",EDGE,"E21.sketch_text.stroke-57"),sQuery(id+"F5.wireOp",EDGE,"E21.sketch_text.stroke-58"),sQuery(id+"F5.wireOp",EDGE,"E21.sketch_text.stroke-59"),sQuery(id+"F5.wireOp",EDGE,"E21.sketch_text.stroke-60"),sQuery(id+"F5.wireOp",EDGE,"E21.sketch_text.stroke-61"),sQuery(id+"F5.wireOp",EDGE,"E21.sketch_text.stroke-62"),sQuery(id+"F5.wireOp",EDGE,"E21.sketch_text.stroke-63"),sQuery(id+"F5.wireOp",EDGE,"E21.sketch_text.stroke-64"),sQuery(id+"F5.wireOp",EDGE,"E21.sketch_text.stroke-65"),sQuery(id+"F5.wireOp",EDGE,"E21.sketch_text.stroke-66"),sQuery(id+"F5.wireOp",EDGE,"E21.sketch_text.stroke-67"),sQuery(id+"F5.wireOp",EDGE,"E21.sketch_text.stroke-68"),sQuery(id+"F5.wireOp",EDGE,"E21.sketch_text.stroke-69"),sQuery(id+"F5.wireOp",EDGE,"E21.sketch_text.stroke-70"),sQuery(id+"F5.wireOp",EDGE,"E21.sketch_text.stroke-71"),sQuery(id+"F5.wireOp",EDGE,"E21.sketch_text.stroke-72"),sQuery(id+"F5.wireOp",EDGE,"E21.sketch_text.stroke-73")])]});
            var Q6;
            Q6=makeQuery(id+"F6.opExtrude","SWEPT_BODY",BODY,{"disambiguationData":[OSD([sQuery(id+"F5.wireOp",EDGE,"E21.sketch_text.stroke-27"),sQuery(id+"F5.wireOp",EDGE,"E21.sketch_text.stroke-28"),sQuery(id+"F5.wireOp",EDGE,"E21.sketch_text.stroke-29"),sQuery(id+"F5.wireOp",EDGE,"E21.sketch_text.stroke-30"),sQuery(id+"F5.wireOp",EDGE,"E21.sketch_text.stroke-31"),sQuery(id+"F5.wireOp",EDGE,"E21.sketch_text.stroke-32"),sQuery(id+"F5.wireOp",EDGE,"E21.sketch_text.stroke-33"),sQuery(id+"F5.wireOp",EDGE,"E21.sketch_text.stroke-34"),sQuery(id+"F5.wireOp",EDGE,"E21.sketch_text.stroke-35"),sQuery(id+"F5.wireOp",EDGE,"E21.sketch_text.stroke-36"),sQuery(id+"F5.wireOp",EDGE,"E21.sketch_text.stroke-37"),sQuery(id+"F5.wireOp",EDGE,"E21.sketch_text.stroke-38"),sQuery(id+"F5.wireOp",EDGE,"E21.sketch_text.stroke-39"),sQuery(id+"F5.wireOp",EDGE,"E21.sketch_text.stroke-40"),sQuery(id+"F5.wireOp",EDGE,"E21.sketch_text.stroke-41"),sQuery(id+"F5.wireOp",EDGE,"E21.sketch_text.stroke-42"),sQuery(id+"F5.wireOp",EDGE,"E21.sketch_text.stroke-43"),sQuery(id+"F5.wireOp",EDGE,"E21.sketch_text.stroke-44"),sQuery(id+"F5.wireOp",EDGE,"E21.sketch_text.stroke-45"),sQuery(id+"F5.wireOp",EDGE,"E21.sketch_text.stroke-46"),sQuery(id+"F5.wireOp",EDGE,"E21.sketch_text.stroke-47"),sQuery(id+"F5.wireOp",EDGE,"E21.sketch_text.stroke-48")])]});
            var Q7;
            Q7=makeQuery(id+"F6.opExtrude","SWEPT_BODY",BODY,{"disambiguationData":[OSD([sQuery(id+"F5.wireOp",EDGE,"E21.sketch_text.stroke-0"),sQuery(id+"F5.wireOp",EDGE,"E21.sketch_text.stroke-1"),sQuery(id+"F5.wireOp",EDGE,"E21.sketch_text.stroke-2"),sQuery(id+"F5.wireOp",EDGE,"E21.sketch_text.stroke-3"),sQuery(id+"F5.wireOp",EDGE,"E21.sketch_text.stroke-4"),sQuery(id+"F5.wireOp",EDGE,"E21.sketch_text.stroke-5"),sQuery(id+"F5.wireOp",EDGE,"E21.sketch_text.stroke-6"),sQuery(id+"F5.wireOp",EDGE,"E21.sketch_text.stroke-7"),sQuery(id+"F5.wireOp",EDGE,"E21.sketch_text.stroke-8"),sQuery(id+"F5.wireOp",EDGE,"E21.sketch_text.stroke-9"),sQuery(id+"F5.wireOp",EDGE,"E21.sketch_text.stroke-10"),sQuery(id+"F5.wireOp",EDGE,"E21.sketch_text.stroke-11"),sQuery(id+"F5.wireOp",EDGE,"E21.sketch_text.stroke-12"),sQuery(id+"F5.wireOp",EDGE,"E21.sketch_text.stroke-13"),sQuery(id+"F5.wireOp",EDGE,"E21.sketch_text.stroke-14"),sQuery(id+"F5.wireOp",EDGE,"E21.sketch_text.stroke-15"),sQuery(id+"F5.wireOp",EDGE,"E21.sketch_text.stroke-16"),sQuery(id+"F5.wireOp",EDGE,"E21.sketch_text.stroke-17"),sQuery(id+"F5.wireOp",EDGE,"E21.sketch_text.stroke-18"),sQuery(id+"F5.wireOp",EDGE,"E21.sketch_text.stroke-19"),sQuery(id+"F5.wireOp",EDGE,"E21.sketch_text.stroke-20"),sQuery(id+"F5.wireOp",EDGE,"E21.sketch_text.stroke-21"),sQuery(id+"F5.wireOp",EDGE,"E21.sketch_text.stroke-22"),sQuery(id+"F5.wireOp",EDGE,"E21.sketch_text.stroke-23"),sQuery(id+"F5.wireOp",EDGE,"E21.sketch_text.stroke-24"),sQuery(id+"F5.wireOp",EDGE,"E21.sketch_text.stroke-25"),sQuery(id+"F5.wireOp",EDGE,"E21.sketch_text.stroke-26")])]});
            var Q8;
            Q8=sQuery(id+"F7.wireOp",EDGE,"E23");
            transform(context, id + "F11", {"entities" : qUnion([Q0, Q1, Q2, Q3, Q4, Q5, Q6, Q7]), "transformType" : TransformType.TRANSLATION_DISTANCE, "transformDirection" : qUnion([Q8]), "distance" : 25.4 * mm, "makeCopy" : false});
        }
        {
            var Q0;
            Q0=qCreatedBy(makeId("Top.planeOp"),FACE);
            var sketch = newSketch(context, id + "F12", { "sketchPlane" : qUnion([Q0])});
            skCircle(sketch, "E25", {"center": v(0, 0) * mm, "radius": 5.77 * mm});
            skCircle(sketch, "E26", {"center": v(0, 0) * mm, "radius": 10.74 * mm});
            skSolve(sketch);
        }
        {
            var Q0;
            Q0=makeQuery(id+"F12.imprint","IMPRINT",FACE,{"disambiguationData":[TD([[makeQuery(id+"F12.imprint","IMPRINT",EDGE,{"derivedFrom":sQuery(id+"F12.wireOp",EDGE,"E25")}),-1.0]])]});
            extrude(context, id + "F13", {"entities" : qUnion([Q0]), "operationType" : NewBodyOperationType.REMOVE, "depth" : 94.97 * mm});
        }
        {
            var Q0;
            Q0=makeQuery(id+"F3.opRevolve","SWEPT_FACE",FACE,{"disambiguationData":[OSD([sQuery(id+"F2.wireOp",EDGE,"E13")])]});
            cPlane(context, id + "F14", {"entities" : qUnion([Q0]), "cplaneType" : CPlaneType.OFFSET, "offset" : 0 * mm, "width" : 152.4 * mm, "height" : 152.4 * mm});
        }
        {
            var Q0;
            Q0=qCreatedBy(id+"F14.planeOp",FACE);
            var sketch = newSketch(context, id + "F15", { "sketchPlane" : qUnion([Q0])});
            skCircle(sketch, "E27", {"center": v(0, 0) * mm, "radius": 2.33 * mm});
            skSolve(sketch);
        }
        {
            var Q0;
            Q0=makeQuery(id+"F15.imprint","IMPRINT",FACE,{"disambiguationData":[TD([[makeQuery(id+"F15.imprint","IMPRINT",EDGE,{"derivedFrom":sQuery(id+"F15.wireOp",EDGE,"E27")}),1.0]])]});
            extrude(context, id + "F16", {"entities" : qUnion([Q0]), "depth" : 4.58 * mm, "hasDraft" : true, "draftAngle" : 18 * degree, "draftPullDirection" : true});
        }
        {
            var Q0;
            Q0=makeQuery(id+"F16.opExtrude","CAP_EDGE",EDGE,{"disambiguationData":[OSD([sQuery(id+"F15.wireOp",EDGE,"E27")])],"isStart":false});
            fillet(context, id + "F17", {"entities" : qUnion([Q0]), "radius" : 0.76 * mm, "tangentPropagation" : true, "allowEdgeOverflow" : false});
        }
    });
